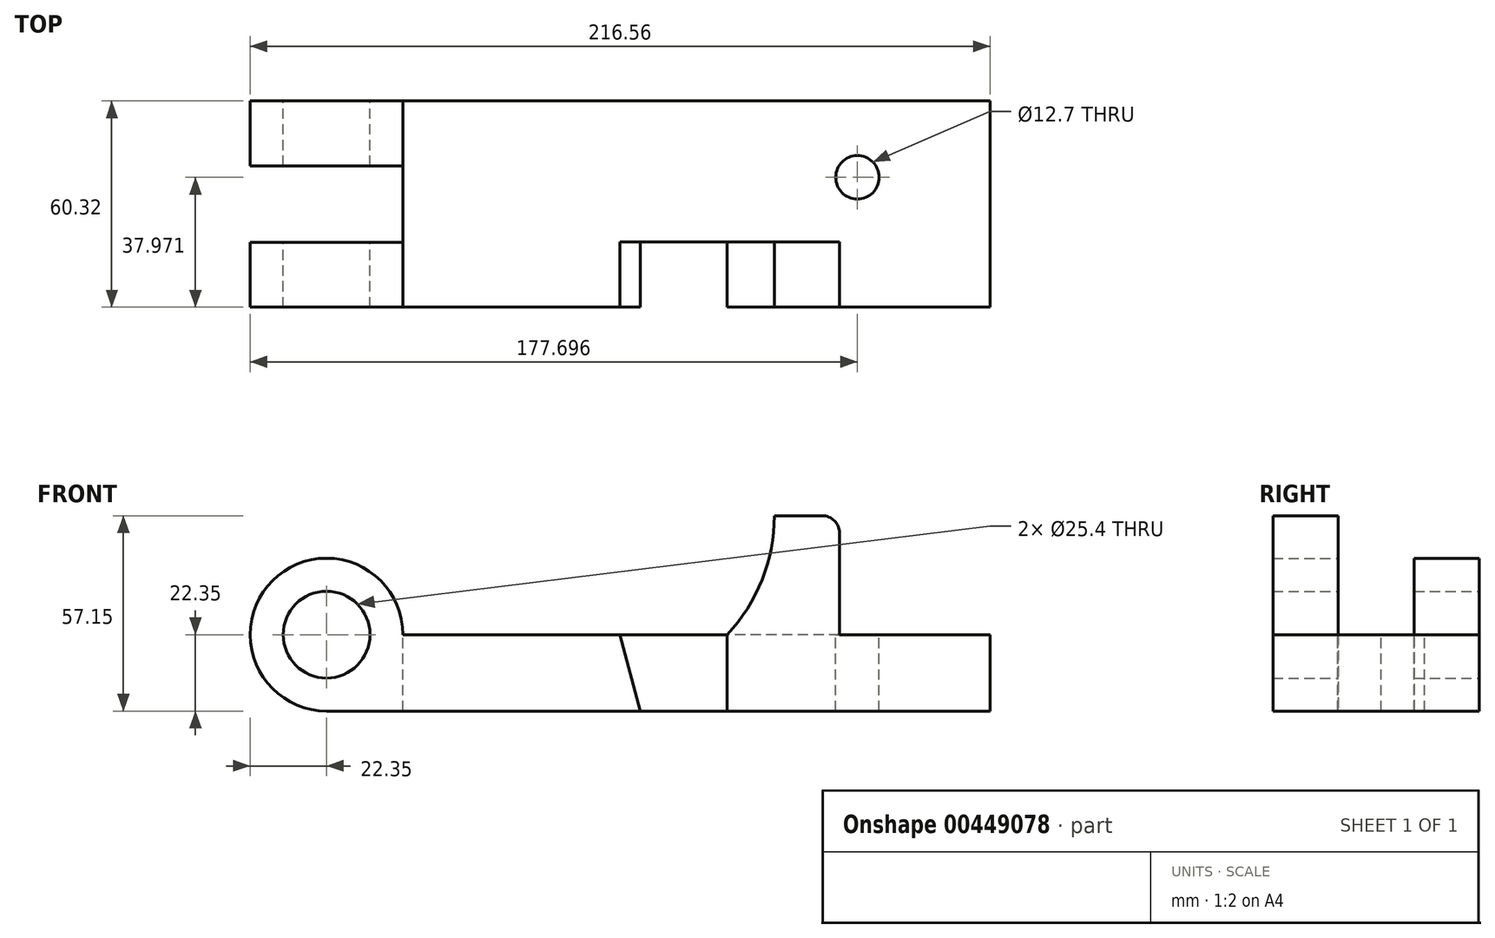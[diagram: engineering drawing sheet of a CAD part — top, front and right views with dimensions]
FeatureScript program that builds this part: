
annotation { "Feature Type Name" : "Feature", "Feature Type Description" : "" }
export const myFeature = defineFeature(function(context is Context, id is Id, definition is map)
    precondition{}
    {
        {
            var Q0;
            Q0=qCreatedBy(makeId("Front.planeOp"),FACE);
            var sketch = newSketch(context, id + "F0", { "sketchPlane" : qUnion([Q0])});
            skCircle(sketch, "E0", {"center": v(0, 0) * mm, "radius": 12.7 * mm});
            skArc(sketch, "E1", {"start": v(22.35, 0) * mm, "mid": v(-15.8, 15.8) * mm, "end": v(0, -22.35) * mm});
            skLineSegment(sketch, "E2", {"start": v(0, -22.35) * mm, "end": v(194.2, -22.35) * mm});
            skLineSegment(sketch, "E3", {"start": v(194.2, -22.35) * mm, "end": v(194.2, 0) * mm});
            skLineSegment(sketch, "E4", {"start": v(194.2, 0) * mm, "end": v(22.35, 0) * mm});
            skSolve(sketch);
        }
        {
            var Q0;
            Q0=makeQuery(id+"F0.imprint","IMPRINT",FACE,{"disambiguationData":[TD([[makeQuery(id+"F0.imprint","IMPRINT",EDGE,{"derivedFrom":sQuery(id+"F0.wireOp",EDGE,"E0")}),-1.0]])]});
            extrude(context, id + "F1", {"entities" : qUnion([Q0]), "endBound" : BoundingType.SYMMETRIC, "depth" : 60.32 * mm});
        }
        {
            var Q0;
            Q0=makeQuery(id+"F1.opExtrude","CAP_FACE",FACE,{"disambiguationData":[OSD([sQuery(id+"F0.wireOp",EDGE,"E0"),sQuery(id+"F0.wireOp",EDGE,"E1"),sQuery(id+"F0.wireOp",EDGE,"E2"),sQuery(id+"F0.wireOp",EDGE,"E3"),sQuery(id+"F0.wireOp",EDGE,"E4")])],"isStart":false});
            var sketch = newSketch(context, id + "F2", { "sketchPlane" : qUnion([Q0])});
            skLineSegment(sketch, "E5.0.0", {"start": v(194.2, -22.35) * mm, "end": v(194.2, -7.87) * mm});
            skLineSegment(sketch, "E5.0.1", {"start": v(186.33, 0) * mm, "end": v(22.35, 0) * mm});
            skArc(sketch, "E5.0.2", {"start": v(22.35, 0) * mm, "mid": v(-15.8, 15.8) * mm, "end": v(0, -22.35) * mm});
            skLineSegment(sketch, "E5.0.3", {"start": v(0, -22.35) * mm, "end": v(194.2, -22.35) * mm});
            skLineSegment(sketch, "E6", {"start": v(85.85, 0) * mm, "end": v(91.85, -22.35) * mm});
            skLineSegment(sketch, "E7", {"start": v(150.09, 0) * mm, "end": v(150.09, -22.35) * mm});
            skPoint(sketch, "E8.visualSharp", {"position": v(194.2, 0) * mm});
            skArc(sketch, "E8.filletArc", {"start": v(194.2, -7.87) * mm, "mid": v(191.9, -2.3) * mm, "end": v(186.33, 0) * mm});
            skSolve(sketch);
        }
        {
            var Q0;
            {var subQ0=sQuery(id+"F2.wireOp",EDGE,"E6");Q0=makeQuery(id+"F2.imprint","IMPRINT",FACE,{"disambiguationData":[TD([[makeQuery(id+"F2.imprint","IMPRINT",EDGE,{"derivedFrom":subQ0}),1.0]])]});}
            extrude(context, id + "F3", {"entities" : qUnion([Q0]), "operationType" : NewBodyOperationType.REMOVE, "oppositeDirection" : true, "depth" : 19.05 * mm});
        }
        {
            var Q0;
            Q0=makeQuery(id+"F3.boolean.opBoolean","COPY",FACE,{"derivedFrom":makeQuery(id+"F3.opExtrude","CAP_FACE",FACE,{"disambiguationData":[OSD([sQuery(id+"F2.wireOp",EDGE,"E5.0.1"),sQuery(id+"F2.wireOp",EDGE,"E5.0.3"),sQuery(id+"F2.wireOp",EDGE,"E6"),sQuery(id+"F2.wireOp",EDGE,"E7")])],"isStart":false})});
            var sketch = newSketch(context, id + "F4", { "sketchPlane" : qUnion([Q0])});
            skLineSegment(sketch, "E9.0.0", {"start": v(150.09, -22.35) * mm, "end": v(150.09, 0) * mm});
            skLineSegment(sketch, "E9.0.1", {"start": v(150.09, 0) * mm, "end": v(85.85, 0) * mm});
            skLineSegment(sketch, "E9.0.2", {"start": v(85.85, 0) * mm, "end": v(91.85, -22.35) * mm});
            skLineSegment(sketch, "E9.0.3", {"start": v(91.85, -22.35) * mm, "end": v(150.09, -22.35) * mm});
            skLineSegment(sketch, "E10", {"start": v(117.25, 0) * mm, "end": v(117.25, -22.35) * mm});
            skArc(sketch, "E11", {"start": v(117.25, 0) * mm, "mid": v(127.46, 16.08) * mm, "end": v(131.04, 34.8) * mm});
            skLineSegment(sketch, "E12", {"start": v(131.04, 34.8) * mm, "end": v(145, 34.8) * mm});
            skLineSegment(sketch, "E13", {"start": v(150.09, 29.72) * mm, "end": v(150.09, 0) * mm});
            skPoint(sketch, "E14.visualSharp", {"position": v(150.09, 34.8) * mm});
            skArc(sketch, "E14.filletArc", {"start": v(150.09, 29.72) * mm, "mid": v(148.6, 33.31) * mm, "end": v(145, 34.8) * mm});
            skSolve(sketch);
        }
        {
            var Q0;
            {var subQ1=sQuery(id+"F4.wireOp",EDGE,"E11");Q0=makeQuery(id+"F4.imprint","IMPRINT",FACE,{"disambiguationData":[TD([[makeQuery(id+"F4.imprint","IMPRINT",EDGE,{"derivedFrom":subQ1}),-1.0]])]});}
            var Q1;
            {var subQ0=sQuery(id+"F4.wireOp",EDGE,"E9.0.0");Q1=makeQuery(id+"F4.imprint","IMPRINT",FACE,{"disambiguationData":[TD([[makeQuery(id+"F4.imprint","IMPRINT",EDGE,{"derivedFrom":subQ0}),-1.0]])]});}
            extrude(context, id + "F5", {"entities" : qUnion([Q0, Q1]), "operationType" : NewBodyOperationType.ADD, "depth" : 19.05 * mm});
        }
        {
            var Q0;
            Q0=qCreatedBy(makeId("Top.planeOp"),FACE);
            var sketch = newSketch(context, id + "F6", { "sketchPlane" : qUnion([Q0])});
            skLineSegment(sketch, "E15", {"start": v(-22.35, -30.16) * mm, "end": v(-22.35, 30.16) * mm});
            skLineSegment(sketch, "E16.0.0", {"start": v(117.25, -11.11) * mm, "end": v(150.09, -11.11) * mm});
            skLineSegment(sketch, "E16.0.1", {"start": v(150.09, -11.11) * mm, "end": v(150.09, -30.16) * mm});
            skLineSegment(sketch, "E16.0.2", {"start": v(150.09, -30.16) * mm, "end": v(194.2, -30.16) * mm});
            skLineSegment(sketch, "E16.0.3", {"start": v(194.2, -30.16) * mm, "end": v(194.2, 30.16) * mm});
            skLineSegment(sketch, "E16.0.4", {"start": v(194.2, 30.16) * mm, "end": v(22.35, 30.16) * mm});
            skLineSegment(sketch, "E16.0.6", {"start": v(22.35, -30.16) * mm, "end": v(85.85, -30.16) * mm});
            skLineSegment(sketch, "E16.0.7", {"start": v(85.85, -30.16) * mm, "end": v(85.85, -11.11) * mm});
            skLineSegment(sketch, "E16.0.8", {"start": v(85.85, -11.11) * mm, "end": v(117.25, -11.11) * mm});
            skLineSegment(sketch, "E17.bottom", {"start": v(-22.35, 11.16) * mm, "end": v(22.35, 11.16) * mm});
            skLineSegment(sketch, "E17.top", {"start": v(-22.35, -11.16) * mm, "end": v(22.35, -11.16) * mm});
            skLineSegment(sketch, "E17.left", {"start": v(-22.35, 11.16) * mm, "end": v(-22.35, -11.16) * mm});
            skLineSegment(sketch, "E17.right", {"start": v(22.35, 11.16) * mm, "end": v(22.35, -11.16) * mm});
            skCircle(sketch, "E18", {"center": v(155.35, 7.81) * mm, "radius": 6.35 * mm});
            skSolve(sketch);
        }
        {
            var Q0;
            Q0=makeQuery(id+"F6.imprint","IMPRINT",FACE,{"disambiguationData":[TD([[makeQuery(id+"F6.imprint","IMPRINT",EDGE,{"derivedFrom":sQuery(id+"F6.wireOp",EDGE,"E18")}),1.0]])]});
            extrude(context, id + "F7", {"entities" : qUnion([Q0]), "operationType" : NewBodyOperationType.REMOVE, "endBound" : BoundingType.THROUGH_ALL, "oppositeDirection" : true, "depth" : 25.4 * mm});
        }
        {
            var Q0;
            Q0=qCreatedBy(makeId("Top.planeOp"),FACE);
            cPlane(context, id + "F8", {"entities" : qUnion([Q0]), "cplaneType" : CPlaneType.OFFSET, "offset" : 127 * mm, "width" : 152.4 * mm, "height" : 152.4 * mm});
        }
        {
            var Q0;
            Q0=qCreatedBy(id+"F8.planeOp",FACE);
            var sketch = newSketch(context, id + "F9", { "sketchPlane" : qUnion([Q0])});
            skLineSegment(sketch, "E19", {"start": v(-22.35, -30.16) * mm, "end": v(-22.35, 30.16) * mm});
            skLineSegment(sketch, "E20.0", {"start": v(-22.35, 11.16) * mm, "end": v(22.35, 11.16) * mm});
            skLineSegment(sketch, "E21.0", {"start": v(-22.35, -11.16) * mm, "end": v(22.35, -11.16) * mm});
            skLineSegment(sketch, "E22.left", {"start": v(-22.35, 11.16) * mm, "end": v(-22.35, -11.16) * mm});
            skLineSegment(sketch, "E22.right", {"start": v(22.35, 11.16) * mm, "end": v(22.35, -11.16) * mm});
            skSolve(sketch);
        }
        {
            var Q0;
            Q0=makeQuery(id+"F9.imprint","IMPRINT",FACE,{"disambiguationData":[TD([[makeQuery(id+"F9.imprint","IMPRINT",EDGE,{"derivedFrom":sQuery(id+"F9.wireOp",EDGE,"E20.0")}),-1.0]])]});
            extrude(context, id + "F10", {"entities" : qUnion([Q0]), "operationType" : NewBodyOperationType.REMOVE, "endBound" : BoundingType.THROUGH_ALL, "oppositeDirection" : true, "depth" : 25.4 * mm});
        }
    });
